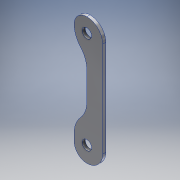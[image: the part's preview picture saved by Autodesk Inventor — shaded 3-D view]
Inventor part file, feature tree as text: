
AUTODESK INVENTOR PART (.ipt)
format: ipt  version: 2016 (Build 200138000, 138)  size: 145,408 bytes
history: native  units: in
note: dims shown in document units (in); Inventor stores cm internally (conversion verified against a paired STEP export)
features: fillet x4, extrude x1, sketch x1
ambient origin geometry x8: Origin, YZ Plane, XZ Plane, XY Plane, X Axis, Y Axis, Z Axis, Center Point
bodies: Solid1 (feature_tree)
feature tree (6):
  extrude  "Extrusion1"  Depth=0.3071in
  fillet  "Fillet9"  Radius=0.0394in
  fillet  "Fillet10"  Radius=0.1575in
  fillet  "Fillet11"  Radius=0.3543in
  fillet  "Fillet12"  Radius=0.3543in
  sketch  "Sketch1"  dims[d0=0.1181in d1=0.1181in d10=0.0394in d11=0.0in d13=0.1575in d14=0.1969in d47=0.3543in d48=0.3543in d49=0.1969in d50=0.1575in d51=0.3071in d52=0.1575in d55=0.1772in d59=1.5748in d60=0.0984in d61=0.0984in d62=0.3071in]
